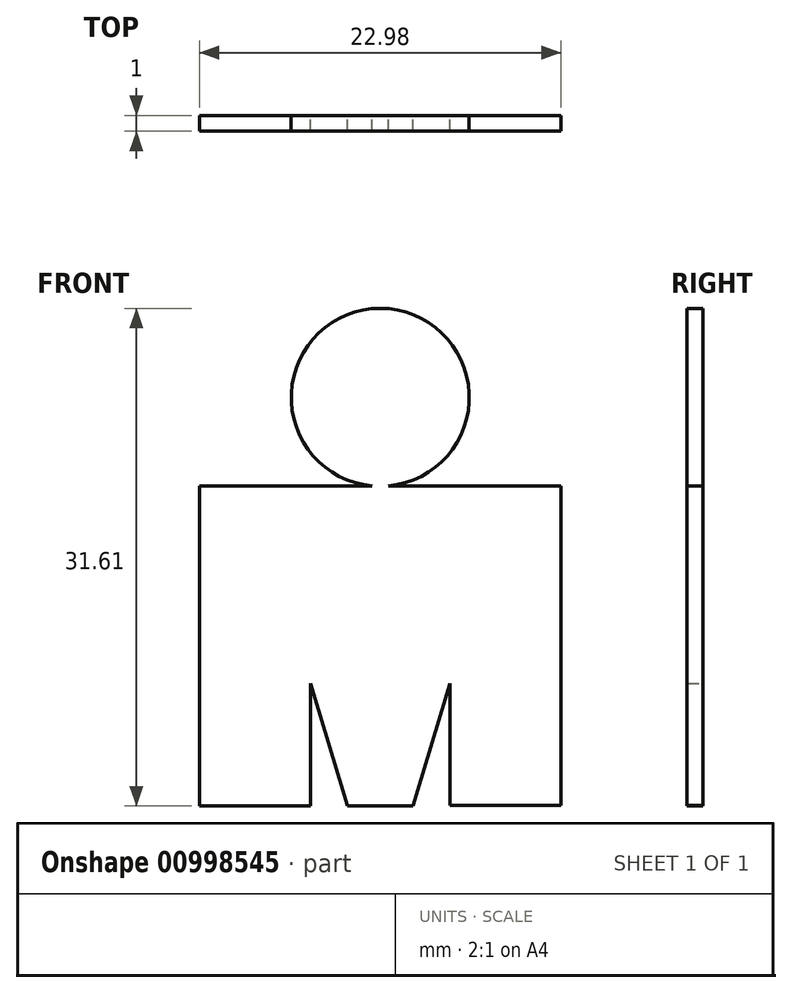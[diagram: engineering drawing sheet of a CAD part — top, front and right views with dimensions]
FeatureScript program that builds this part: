
annotation { "Feature Type Name" : "Feature", "Feature Type Description" : "" }
export const myFeature = defineFeature(function(context is Context, id is Id, definition is map)
    precondition{}
    {
        {
            var Q0;
            Q0=qCreatedBy(makeId("Front.planeOp"),FACE);
            var sketch = newSketch(context, id + "F0", { "sketchPlane" : qUnion([Q0])});
            skCircle(sketch, "E0", {"center": v(0, 25.96) * mm, "radius": 5.65 * mm});
            skLineSegment(sketch, "E1.bottom", {"start": v(-11.49, 20.33) * mm, "end": v(11.49, 20.33) * mm});
            skLineSegment(sketch, "E1.top", {"start": v(-11.49, -93.39) * mm, "end": v(11.49, -93.39) * mm});
            skLineSegment(sketch, "E2", {"start": v(-4.42, 7.8) * mm, "end": v(-2.07, 0) * mm});
            skPoint(sketch, "E3.endSnap0", {"position": v(0, -93.39) * mm});
            skLineSegment(sketch, "E4.MirrorCS", {"start": v(4.42, 7.8) * mm, "end": v(2.07, 0) * mm});
            skLineSegment(sketch, "E5", {"start": v(-4.42, -74.33) * mm, "end": v(4.42, -74.33) * mm});
            skLineSegment(sketch, "E6", {"start": v(-2.07, -68.69) * mm, "end": v(2.07, -68.69) * mm});
            skLineSegment(sketch, "E7", {"start": v(-11.49, 0) * mm, "end": v(-4.42, 0) * mm});
            skLineSegment(sketch, "E8", {"start": v(-2.07, 0) * mm, "end": v(2.07, 0) * mm});
            skLineSegment(sketch, "E9", {"start": v(4.42, 0.05) * mm, "end": v(11.49, 0.05) * mm});
            skLineSegment(sketch, "E10", {"start": v(-11.49, 0) * mm, "end": v(-11.49, 20.33) * mm});
            skLineSegment(sketch, "E11", {"start": v(11.49, 20.33) * mm, "end": v(-11.49, 20.33) * mm});
            skLineSegment(sketch, "E12", {"start": v(11.49, 20.33) * mm, "end": v(11.49, 0.05) * mm});
            skLineSegment(sketch, "E13", {"start": v(4.42, 7.8) * mm, "end": v(4.42, 0.05) * mm});
            skLineSegment(sketch, "E14", {"start": v(-2.07, 0) * mm, "end": v(-4.42, 7.8) * mm});
            skLineSegment(sketch, "E15", {"start": v(-4.42, 0) * mm, "end": v(-4.42, 7.8) * mm});
            skSolve(sketch);
        }
        {
            var Q0;
            Q0 = qSketchRegion(id + "F0", true);
            extrude(context, id + "F1", {"entities" : qUnion([Q0]), "depth" : 1 * mm, "offsetDistance" : 25 * mm});
        }
    });
